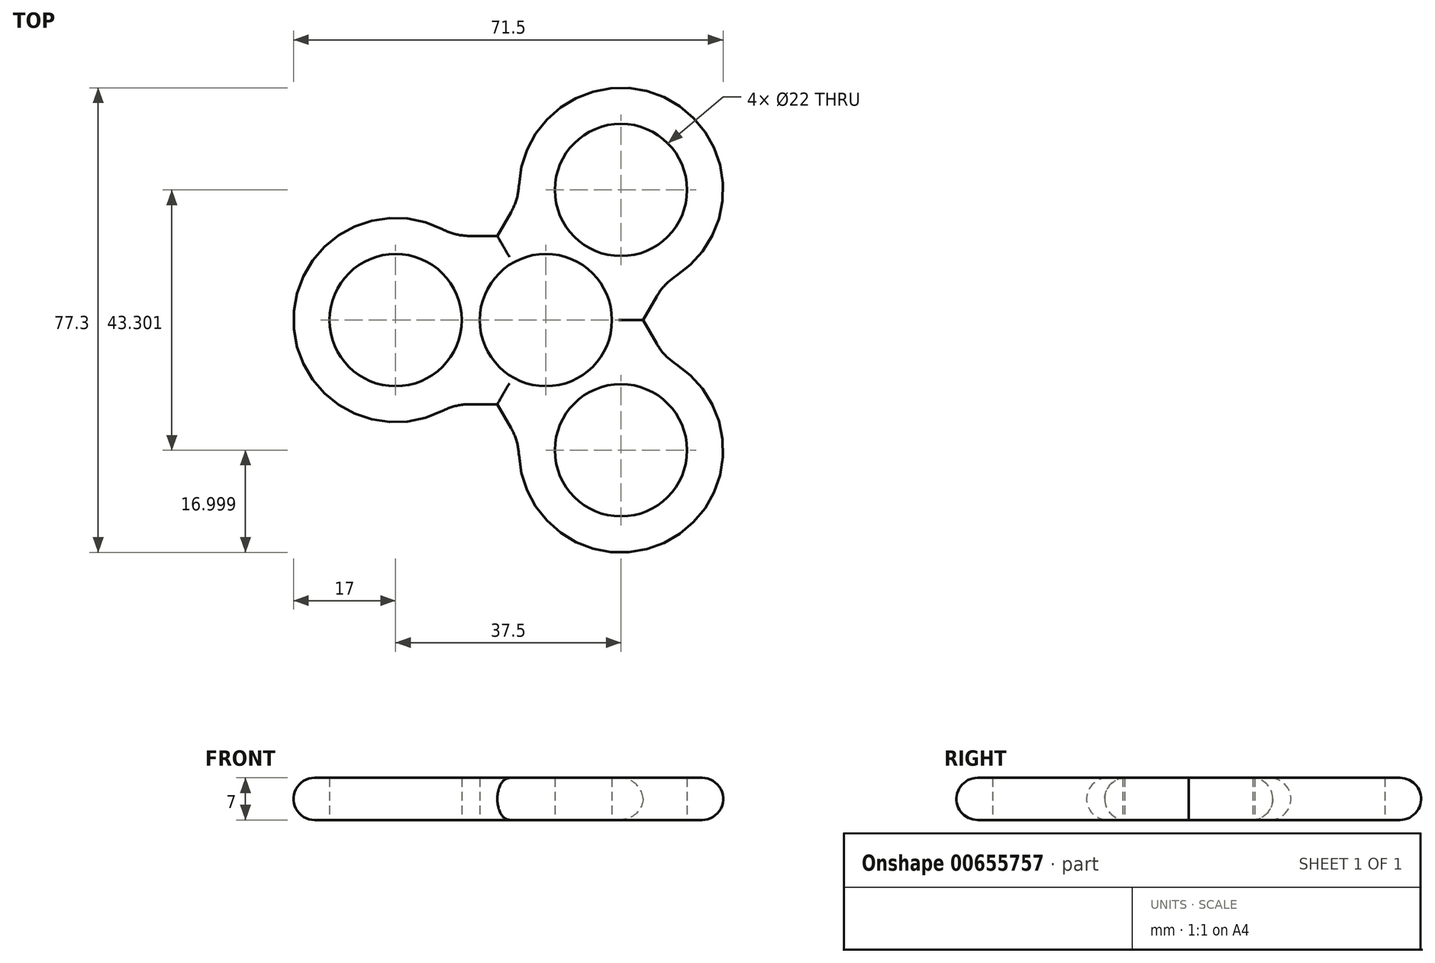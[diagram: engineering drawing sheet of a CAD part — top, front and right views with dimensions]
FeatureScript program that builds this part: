
annotation { "Feature Type Name" : "Feature", "Feature Type Description" : "" }
export const myFeature = defineFeature(function(context is Context, id is Id, definition is map)
    precondition{}
    {
        {
            var Q0;
            Q0=qCreatedBy(makeId("Top.planeOp"),FACE);
            var sketch = newSketch(context, id + "F0", { "sketchPlane" : qUnion([Q0])});
            skArc(sketch, "E0", {"start": v(0, 11) * mm, "mid": v(-11, 0) * mm, "end": v(0, -11) * mm});
            skLineSegment(sketch, "E1", {"start": v(0, 56.07) * mm, "end": v(0, 11) * mm, "construction": true});
            skLineSegment(sketch, "E2", {"start": v(-42, 56.32) * mm, "end": v(-42, -55.95) * mm, "construction": true});
            skArc(sketch, "E3", {"start": v(-15.36, 14) * mm, "mid": v(-42, 0) * mm, "end": v(-15.36, -14) * mm});
            skLineSegment(sketch, "E4", {"start": v(0, 14) * mm, "end": v(-15.36, 14) * mm});
            skLineSegment(sketch, "E5", {"start": v(0, -14) * mm, "end": v(-15.36, -14) * mm});
            skLineSegment(sketch, "E6", {"start": v(0, 14) * mm, "end": v(0, 11) * mm});
            skLineSegment(sketch, "E7.trimOffspring", {"start": v(0, -11) * mm, "end": v(0, -55.82) * mm, "construction": true});
            skLineSegment(sketch, "E8.trimOffspring", {"start": v(0, -11) * mm, "end": v(0, -14) * mm});
            skCircle(sketch, "E9", {"center": v(-25, 0) * mm, "radius": 11 * mm});
            skSolve(sketch);
        }
        {
            var Q0;
            Q0=qSketchRegion(id+"F0",true);
            extrude(context, id + "F1", {"entities" : qUnion([Q0]), "depth" : 7 * mm, "offsetDistance" : 25 * mm});
        }
        {
            var Q0;
            Q0=makeQuery(id+"F1.opExtrude","SWEPT_EDGE",EDGE,{"disambiguationData":[OSD([sQuery(id+"F0.wireOp",EDGE,"E3"),sQuery(id+"F0.wireOp",EDGE,"E5")])]});
            var Q1;
            Q1=makeQuery(id+"F1.opExtrude","SWEPT_EDGE",EDGE,{"disambiguationData":[OSD([sQuery(id+"F0.wireOp",EDGE,"E3"),sQuery(id+"F0.wireOp",EDGE,"E4")])]});
            fillet(context, id + "F2", {"entities" : qUnion([Q0, Q1]), "radius" : 10 * mm, "tangentPropagation" : true, "allowEdgeOverflow" : false});
        }
        {
            var Q0;
            Q0=qCreatedBy(makeId("Front.planeOp"),FACE);
            var sketch = newSketch(context, id + "F3", { "sketchPlane" : qUnion([Q0])});
            skLineSegment(sketch, "E10.0", {"start": v(0, 7) * mm, "end": v(0, 0) * mm});
            skSolve(sketch);
        }
        {
            var Q0;
            Q0=makeQuery(id+"F1.opExtrude","SWEPT_BODY",BODY,{"disambiguationData":[OSD([sQuery(id+"F0.wireOp",EDGE,"E0"),sQuery(id+"F0.wireOp",EDGE,"E3"),sQuery(id+"F0.wireOp",EDGE,"E4"),sQuery(id+"F0.wireOp",EDGE,"E5"),sQuery(id+"F0.wireOp",EDGE,"E6"),sQuery(id+"F0.wireOp",EDGE,"E8.trimOffspring"),sQuery(id+"F0.wireOp",EDGE,"E9")])]});
            var Q1;
            Q1=sQuery(id+"F3.wireOp",EDGE,"E10.0");
            circularPattern(context, id + "F4", {"operationType" : NewBodyOperationType.ADD, "entities" : qUnion([Q0]), "axis" : qUnion([Q1]), "angle" : 240 * degree, "instanceCount" : 3, "equalSpace" : true});
        }
        {
            var Q0;
            Q0=makeQuery(id+"F1.opExtrude","CAP_EDGE",EDGE,{"disambiguationData":[OSD([sQuery(id+"F0.wireOp",EDGE,"E3")])],"isStart":false});
            var Q1;
            {var subQ0=sQuery(id+"F0.wireOp",EDGE,"E4");var subQ1=sQuery(id+"F0.wireOp",EDGE,"E3");Q1=makeQuery(id+"F2.opFillet","BLEND_EDGE",EDGE,{"blendedFrom":[makeQuery(id+"F1.opExtrude","SWEPT_EDGE",EDGE,{"disambiguationData":[OSD([subQ1,subQ0])]}),makeQuery(id+"F1.opExtrude","CAP_FACE",FACE,{"disambiguationData":[OSD([sQuery(id+"F0.wireOp",EDGE,"E0"),subQ1,subQ0,sQuery(id+"F0.wireOp",EDGE,"E5"),sQuery(id+"F0.wireOp",EDGE,"E6"),sQuery(id+"F0.wireOp",EDGE,"E8.trimOffspring"),sQuery(id+"F0.wireOp",EDGE,"E9")])],"isStart":false})],"blendedInto":[makeQuery(id+"F1.opExtrude","CAP_FACE",FACE,{"disambiguationData":[OSD([sQuery(id+"F0.wireOp",EDGE,"E0"),subQ1,subQ0,sQuery(id+"F0.wireOp",EDGE,"E5"),sQuery(id+"F0.wireOp",EDGE,"E6"),sQuery(id+"F0.wireOp",EDGE,"E8.trimOffspring"),sQuery(id+"F0.wireOp",EDGE,"E9")])],"isStart":false})]});}
            var Q2;
            Q2=makeQuery(id+"F1.opExtrude","CAP_EDGE",EDGE,{"disambiguationData":[OSD([sQuery(id+"F0.wireOp",EDGE,"E4")])],"isStart":false});
            var Q3;
            Q3=makeQuery(id+"F4.opPattern","COPY",EDGE,{"derivedFrom":makeQuery(id+"F1.opExtrude","CAP_EDGE",EDGE,{"disambiguationData":[OSD([sQuery(id+"F0.wireOp",EDGE,"E5")])],"isStart":false}),"instanceName":"1"});
            var Q4;
            {var subQ0=sQuery(id+"F0.wireOp",EDGE,"E5");var subQ1=sQuery(id+"F0.wireOp",EDGE,"E3");Q4=makeQuery(id+"F2.opFillet","BLEND_EDGE",EDGE,{"blendedFrom":[makeQuery(id+"F1.opExtrude","SWEPT_EDGE",EDGE,{"disambiguationData":[OSD([subQ1,subQ0])]}),makeQuery(id+"F1.opExtrude","CAP_FACE",FACE,{"disambiguationData":[OSD([sQuery(id+"F0.wireOp",EDGE,"E0"),subQ1,sQuery(id+"F0.wireOp",EDGE,"E4"),subQ0,sQuery(id+"F0.wireOp",EDGE,"E6"),sQuery(id+"F0.wireOp",EDGE,"E8.trimOffspring"),sQuery(id+"F0.wireOp",EDGE,"E9")])],"isStart":false})],"blendedInto":[makeQuery(id+"F1.opExtrude","CAP_FACE",FACE,{"disambiguationData":[OSD([sQuery(id+"F0.wireOp",EDGE,"E0"),subQ1,sQuery(id+"F0.wireOp",EDGE,"E4"),subQ0,sQuery(id+"F0.wireOp",EDGE,"E6"),sQuery(id+"F0.wireOp",EDGE,"E8.trimOffspring"),sQuery(id+"F0.wireOp",EDGE,"E9")])],"isStart":false})]});}
            var Q5;
            Q5=makeQuery(id+"F1.opExtrude","CAP_EDGE",EDGE,{"disambiguationData":[OSD([sQuery(id+"F0.wireOp",EDGE,"E5")])],"isStart":false});
            var Q6;
            Q6=makeQuery(id+"F4.opPattern","COPY",EDGE,{"derivedFrom":makeQuery(id+"F1.opExtrude","CAP_EDGE",EDGE,{"disambiguationData":[OSD([sQuery(id+"F0.wireOp",EDGE,"E4")])],"isStart":false}),"instanceName":"2"});
            var Q7;
            {var subQ0=sQuery(id+"F0.wireOp",EDGE,"E4");var subQ1=sQuery(id+"F0.wireOp",EDGE,"E3");Q7=makeQuery(id+"F4.opPattern","COPY",EDGE,{"derivedFrom":makeQuery(id+"F2.opFillet","BLEND_EDGE",EDGE,{"blendedFrom":[makeQuery(id+"F1.opExtrude","SWEPT_EDGE",EDGE,{"disambiguationData":[OSD([subQ1,subQ0])]}),makeQuery(id+"F1.opExtrude","CAP_FACE",FACE,{"disambiguationData":[OSD([sQuery(id+"F0.wireOp",EDGE,"E0"),subQ1,subQ0,sQuery(id+"F0.wireOp",EDGE,"E5"),sQuery(id+"F0.wireOp",EDGE,"E6"),sQuery(id+"F0.wireOp",EDGE,"E8.trimOffspring"),sQuery(id+"F0.wireOp",EDGE,"E9")])],"isStart":false})],"blendedInto":[makeQuery(id+"F1.opExtrude","CAP_FACE",FACE,{"disambiguationData":[OSD([sQuery(id+"F0.wireOp",EDGE,"E0"),subQ1,subQ0,sQuery(id+"F0.wireOp",EDGE,"E5"),sQuery(id+"F0.wireOp",EDGE,"E6"),sQuery(id+"F0.wireOp",EDGE,"E8.trimOffspring"),sQuery(id+"F0.wireOp",EDGE,"E9")])],"isStart":false})]}),"instanceName":"2"});}
            var Q8;
            Q8=makeQuery(id+"F4.opPattern","COPY",EDGE,{"derivedFrom":makeQuery(id+"F1.opExtrude","CAP_EDGE",EDGE,{"disambiguationData":[OSD([sQuery(id+"F0.wireOp",EDGE,"E3")])],"isStart":false}),"instanceName":"2"});
            var Q9;
            {var subQ0=sQuery(id+"F0.wireOp",EDGE,"E5");var subQ1=sQuery(id+"F0.wireOp",EDGE,"E3");Q9=makeQuery(id+"F4.opPattern","COPY",EDGE,{"derivedFrom":makeQuery(id+"F2.opFillet","BLEND_EDGE",EDGE,{"blendedFrom":[makeQuery(id+"F1.opExtrude","SWEPT_EDGE",EDGE,{"disambiguationData":[OSD([subQ1,subQ0])]}),makeQuery(id+"F1.opExtrude","CAP_FACE",FACE,{"disambiguationData":[OSD([sQuery(id+"F0.wireOp",EDGE,"E0"),subQ1,sQuery(id+"F0.wireOp",EDGE,"E4"),subQ0,sQuery(id+"F0.wireOp",EDGE,"E6"),sQuery(id+"F0.wireOp",EDGE,"E8.trimOffspring"),sQuery(id+"F0.wireOp",EDGE,"E9")])],"isStart":false})],"blendedInto":[makeQuery(id+"F1.opExtrude","CAP_FACE",FACE,{"disambiguationData":[OSD([sQuery(id+"F0.wireOp",EDGE,"E0"),subQ1,sQuery(id+"F0.wireOp",EDGE,"E4"),subQ0,sQuery(id+"F0.wireOp",EDGE,"E6"),sQuery(id+"F0.wireOp",EDGE,"E8.trimOffspring"),sQuery(id+"F0.wireOp",EDGE,"E9")])],"isStart":false})]}),"instanceName":"2"});}
            var Q10;
            Q10=makeQuery(id+"F4.opPattern","COPY",EDGE,{"derivedFrom":makeQuery(id+"F1.opExtrude","CAP_EDGE",EDGE,{"disambiguationData":[OSD([sQuery(id+"F0.wireOp",EDGE,"E5")])],"isStart":false}),"instanceName":"2"});
            var Q11;
            Q11=makeQuery(id+"F4.opPattern","COPY",EDGE,{"derivedFrom":makeQuery(id+"F1.opExtrude","CAP_EDGE",EDGE,{"disambiguationData":[OSD([sQuery(id+"F0.wireOp",EDGE,"E4")])],"isStart":false}),"instanceName":"1"});
            var Q12;
            {var subQ0=sQuery(id+"F0.wireOp",EDGE,"E4");var subQ1=sQuery(id+"F0.wireOp",EDGE,"E3");Q12=makeQuery(id+"F4.opPattern","COPY",EDGE,{"derivedFrom":makeQuery(id+"F2.opFillet","BLEND_EDGE",EDGE,{"blendedFrom":[makeQuery(id+"F1.opExtrude","SWEPT_EDGE",EDGE,{"disambiguationData":[OSD([subQ1,subQ0])]}),makeQuery(id+"F1.opExtrude","CAP_FACE",FACE,{"disambiguationData":[OSD([sQuery(id+"F0.wireOp",EDGE,"E0"),subQ1,subQ0,sQuery(id+"F0.wireOp",EDGE,"E5"),sQuery(id+"F0.wireOp",EDGE,"E6"),sQuery(id+"F0.wireOp",EDGE,"E8.trimOffspring"),sQuery(id+"F0.wireOp",EDGE,"E9")])],"isStart":false})],"blendedInto":[makeQuery(id+"F1.opExtrude","CAP_FACE",FACE,{"disambiguationData":[OSD([sQuery(id+"F0.wireOp",EDGE,"E0"),subQ1,subQ0,sQuery(id+"F0.wireOp",EDGE,"E5"),sQuery(id+"F0.wireOp",EDGE,"E6"),sQuery(id+"F0.wireOp",EDGE,"E8.trimOffspring"),sQuery(id+"F0.wireOp",EDGE,"E9")])],"isStart":false})]}),"instanceName":"1"});}
            var Q13;
            Q13=makeQuery(id+"F4.opPattern","COPY",EDGE,{"derivedFrom":makeQuery(id+"F1.opExtrude","CAP_EDGE",EDGE,{"disambiguationData":[OSD([sQuery(id+"F0.wireOp",EDGE,"E3")])],"isStart":false}),"instanceName":"1"});
            var Q14;
            {var subQ0=sQuery(id+"F0.wireOp",EDGE,"E5");var subQ1=sQuery(id+"F0.wireOp",EDGE,"E3");Q14=makeQuery(id+"F4.opPattern","COPY",EDGE,{"derivedFrom":makeQuery(id+"F2.opFillet","BLEND_EDGE",EDGE,{"blendedFrom":[makeQuery(id+"F1.opExtrude","SWEPT_EDGE",EDGE,{"disambiguationData":[OSD([subQ1,subQ0])]}),makeQuery(id+"F1.opExtrude","CAP_FACE",FACE,{"disambiguationData":[OSD([sQuery(id+"F0.wireOp",EDGE,"E0"),subQ1,sQuery(id+"F0.wireOp",EDGE,"E4"),subQ0,sQuery(id+"F0.wireOp",EDGE,"E6"),sQuery(id+"F0.wireOp",EDGE,"E8.trimOffspring"),sQuery(id+"F0.wireOp",EDGE,"E9")])],"isStart":false})],"blendedInto":[makeQuery(id+"F1.opExtrude","CAP_FACE",FACE,{"disambiguationData":[OSD([sQuery(id+"F0.wireOp",EDGE,"E0"),subQ1,sQuery(id+"F0.wireOp",EDGE,"E4"),subQ0,sQuery(id+"F0.wireOp",EDGE,"E6"),sQuery(id+"F0.wireOp",EDGE,"E8.trimOffspring"),sQuery(id+"F0.wireOp",EDGE,"E9")])],"isStart":false})]}),"instanceName":"1"});}
            fillet(context, id + "F5", {"entities" : qUnion([Q0, Q1, Q2, Q3, Q4, Q5, Q6, Q7, Q8, Q9, Q10, Q11, Q12, Q13, Q14]), "radius" : 3.5 * mm, "tangentPropagation" : true, "allowEdgeOverflow" : false});
        }
        {
            var Q0;
            {var subQ0=sQuery(id+"F0.wireOp",EDGE,"E4");var subQ1=sQuery(id+"F0.wireOp",EDGE,"E3");Q0=makeQuery(id+"F4.opPattern","COPY",EDGE,{"derivedFrom":makeQuery(id+"F2.opFillet","BLEND_EDGE",EDGE,{"blendedFrom":[makeQuery(id+"F1.opExtrude","SWEPT_EDGE",EDGE,{"disambiguationData":[OSD([subQ1,subQ0])]}),makeQuery(id+"F1.opExtrude","CAP_FACE",FACE,{"disambiguationData":[OSD([sQuery(id+"F0.wireOp",EDGE,"E0"),subQ1,subQ0,sQuery(id+"F0.wireOp",EDGE,"E5"),sQuery(id+"F0.wireOp",EDGE,"E6"),sQuery(id+"F0.wireOp",EDGE,"E8.trimOffspring"),sQuery(id+"F0.wireOp",EDGE,"E9")])],"isStart":true})],"blendedInto":[makeQuery(id+"F1.opExtrude","CAP_FACE",FACE,{"disambiguationData":[OSD([sQuery(id+"F0.wireOp",EDGE,"E0"),subQ1,subQ0,sQuery(id+"F0.wireOp",EDGE,"E5"),sQuery(id+"F0.wireOp",EDGE,"E6"),sQuery(id+"F0.wireOp",EDGE,"E8.trimOffspring"),sQuery(id+"F0.wireOp",EDGE,"E9")])],"isStart":true})]}),"instanceName":"1"});}
            var Q1;
            Q1=makeQuery(id+"F4.opPattern","COPY",EDGE,{"derivedFrom":makeQuery(id+"F1.opExtrude","CAP_EDGE",EDGE,{"disambiguationData":[OSD([sQuery(id+"F0.wireOp",EDGE,"E4")])],"isStart":true}),"instanceName":"1"});
            var Q2;
            Q2=makeQuery(id+"F4.opPattern","COPY",EDGE,{"derivedFrom":makeQuery(id+"F1.opExtrude","CAP_EDGE",EDGE,{"disambiguationData":[OSD([sQuery(id+"F0.wireOp",EDGE,"E5")])],"isStart":true}),"instanceName":"2"});
            var Q3;
            {var subQ0=sQuery(id+"F0.wireOp",EDGE,"E5");var subQ1=sQuery(id+"F0.wireOp",EDGE,"E3");Q3=makeQuery(id+"F4.opPattern","COPY",EDGE,{"derivedFrom":makeQuery(id+"F2.opFillet","BLEND_EDGE",EDGE,{"blendedFrom":[makeQuery(id+"F1.opExtrude","SWEPT_EDGE",EDGE,{"disambiguationData":[OSD([subQ1,subQ0])]}),makeQuery(id+"F1.opExtrude","CAP_FACE",FACE,{"disambiguationData":[OSD([sQuery(id+"F0.wireOp",EDGE,"E0"),subQ1,sQuery(id+"F0.wireOp",EDGE,"E4"),subQ0,sQuery(id+"F0.wireOp",EDGE,"E6"),sQuery(id+"F0.wireOp",EDGE,"E8.trimOffspring"),sQuery(id+"F0.wireOp",EDGE,"E9")])],"isStart":true})],"blendedInto":[makeQuery(id+"F1.opExtrude","CAP_FACE",FACE,{"disambiguationData":[OSD([sQuery(id+"F0.wireOp",EDGE,"E0"),subQ1,sQuery(id+"F0.wireOp",EDGE,"E4"),subQ0,sQuery(id+"F0.wireOp",EDGE,"E6"),sQuery(id+"F0.wireOp",EDGE,"E8.trimOffspring"),sQuery(id+"F0.wireOp",EDGE,"E9")])],"isStart":true})]}),"instanceName":"2"});}
            var Q4;
            Q4=makeQuery(id+"F4.opPattern","COPY",EDGE,{"derivedFrom":makeQuery(id+"F1.opExtrude","CAP_EDGE",EDGE,{"disambiguationData":[OSD([sQuery(id+"F0.wireOp",EDGE,"E3")])],"isStart":true}),"instanceName":"2"});
            var Q5;
            {var subQ0=sQuery(id+"F0.wireOp",EDGE,"E4");var subQ1=sQuery(id+"F0.wireOp",EDGE,"E3");Q5=makeQuery(id+"F4.opPattern","COPY",EDGE,{"derivedFrom":makeQuery(id+"F2.opFillet","BLEND_EDGE",EDGE,{"blendedFrom":[makeQuery(id+"F1.opExtrude","SWEPT_EDGE",EDGE,{"disambiguationData":[OSD([subQ1,subQ0])]}),makeQuery(id+"F1.opExtrude","CAP_FACE",FACE,{"disambiguationData":[OSD([sQuery(id+"F0.wireOp",EDGE,"E0"),subQ1,subQ0,sQuery(id+"F0.wireOp",EDGE,"E5"),sQuery(id+"F0.wireOp",EDGE,"E6"),sQuery(id+"F0.wireOp",EDGE,"E8.trimOffspring"),sQuery(id+"F0.wireOp",EDGE,"E9")])],"isStart":true})],"blendedInto":[makeQuery(id+"F1.opExtrude","CAP_FACE",FACE,{"disambiguationData":[OSD([sQuery(id+"F0.wireOp",EDGE,"E0"),subQ1,subQ0,sQuery(id+"F0.wireOp",EDGE,"E5"),sQuery(id+"F0.wireOp",EDGE,"E6"),sQuery(id+"F0.wireOp",EDGE,"E8.trimOffspring"),sQuery(id+"F0.wireOp",EDGE,"E9")])],"isStart":true})]}),"instanceName":"2"});}
            var Q6;
            Q6=makeQuery(id+"F4.opPattern","COPY",EDGE,{"derivedFrom":makeQuery(id+"F1.opExtrude","CAP_EDGE",EDGE,{"disambiguationData":[OSD([sQuery(id+"F0.wireOp",EDGE,"E4")])],"isStart":true}),"instanceName":"2"});
            var Q7;
            Q7=makeQuery(id+"F1.opExtrude","CAP_EDGE",EDGE,{"disambiguationData":[OSD([sQuery(id+"F0.wireOp",EDGE,"E5")])],"isStart":true});
            var Q8;
            {var subQ0=sQuery(id+"F0.wireOp",EDGE,"E5");var subQ1=sQuery(id+"F0.wireOp",EDGE,"E3");Q8=makeQuery(id+"F2.opFillet","BLEND_EDGE",EDGE,{"blendedFrom":[makeQuery(id+"F1.opExtrude","SWEPT_EDGE",EDGE,{"disambiguationData":[OSD([subQ1,subQ0])]}),makeQuery(id+"F1.opExtrude","CAP_FACE",FACE,{"disambiguationData":[OSD([sQuery(id+"F0.wireOp",EDGE,"E0"),subQ1,sQuery(id+"F0.wireOp",EDGE,"E4"),subQ0,sQuery(id+"F0.wireOp",EDGE,"E6"),sQuery(id+"F0.wireOp",EDGE,"E8.trimOffspring"),sQuery(id+"F0.wireOp",EDGE,"E9")])],"isStart":true})],"blendedInto":[makeQuery(id+"F1.opExtrude","CAP_FACE",FACE,{"disambiguationData":[OSD([sQuery(id+"F0.wireOp",EDGE,"E0"),subQ1,sQuery(id+"F0.wireOp",EDGE,"E4"),subQ0,sQuery(id+"F0.wireOp",EDGE,"E6"),sQuery(id+"F0.wireOp",EDGE,"E8.trimOffspring"),sQuery(id+"F0.wireOp",EDGE,"E9")])],"isStart":true})]});}
            var Q9;
            Q9=makeQuery(id+"F1.opExtrude","CAP_EDGE",EDGE,{"disambiguationData":[OSD([sQuery(id+"F0.wireOp",EDGE,"E3")])],"isStart":true});
            var Q10;
            {var subQ0=sQuery(id+"F0.wireOp",EDGE,"E4");var subQ1=sQuery(id+"F0.wireOp",EDGE,"E3");Q10=makeQuery(id+"F2.opFillet","BLEND_EDGE",EDGE,{"blendedFrom":[makeQuery(id+"F1.opExtrude","SWEPT_EDGE",EDGE,{"disambiguationData":[OSD([subQ1,subQ0])]}),makeQuery(id+"F1.opExtrude","CAP_FACE",FACE,{"disambiguationData":[OSD([sQuery(id+"F0.wireOp",EDGE,"E0"),subQ1,subQ0,sQuery(id+"F0.wireOp",EDGE,"E5"),sQuery(id+"F0.wireOp",EDGE,"E6"),sQuery(id+"F0.wireOp",EDGE,"E8.trimOffspring"),sQuery(id+"F0.wireOp",EDGE,"E9")])],"isStart":true})],"blendedInto":[makeQuery(id+"F1.opExtrude","CAP_FACE",FACE,{"disambiguationData":[OSD([sQuery(id+"F0.wireOp",EDGE,"E0"),subQ1,subQ0,sQuery(id+"F0.wireOp",EDGE,"E5"),sQuery(id+"F0.wireOp",EDGE,"E6"),sQuery(id+"F0.wireOp",EDGE,"E8.trimOffspring"),sQuery(id+"F0.wireOp",EDGE,"E9")])],"isStart":true})]});}
            var Q11;
            Q11=makeQuery(id+"F1.opExtrude","CAP_EDGE",EDGE,{"disambiguationData":[OSD([sQuery(id+"F0.wireOp",EDGE,"E4")])],"isStart":true});
            var Q12;
            Q12=makeQuery(id+"F4.opPattern","COPY",EDGE,{"derivedFrom":makeQuery(id+"F1.opExtrude","CAP_EDGE",EDGE,{"disambiguationData":[OSD([sQuery(id+"F0.wireOp",EDGE,"E5")])],"isStart":true}),"instanceName":"1"});
            var Q13;
            {var subQ0=sQuery(id+"F0.wireOp",EDGE,"E5");var subQ1=sQuery(id+"F0.wireOp",EDGE,"E3");Q13=makeQuery(id+"F4.opPattern","COPY",EDGE,{"derivedFrom":makeQuery(id+"F2.opFillet","BLEND_EDGE",EDGE,{"blendedFrom":[makeQuery(id+"F1.opExtrude","SWEPT_EDGE",EDGE,{"disambiguationData":[OSD([subQ1,subQ0])]}),makeQuery(id+"F1.opExtrude","CAP_FACE",FACE,{"disambiguationData":[OSD([sQuery(id+"F0.wireOp",EDGE,"E0"),subQ1,sQuery(id+"F0.wireOp",EDGE,"E4"),subQ0,sQuery(id+"F0.wireOp",EDGE,"E6"),sQuery(id+"F0.wireOp",EDGE,"E8.trimOffspring"),sQuery(id+"F0.wireOp",EDGE,"E9")])],"isStart":true})],"blendedInto":[makeQuery(id+"F1.opExtrude","CAP_FACE",FACE,{"disambiguationData":[OSD([sQuery(id+"F0.wireOp",EDGE,"E0"),subQ1,sQuery(id+"F0.wireOp",EDGE,"E4"),subQ0,sQuery(id+"F0.wireOp",EDGE,"E6"),sQuery(id+"F0.wireOp",EDGE,"E8.trimOffspring"),sQuery(id+"F0.wireOp",EDGE,"E9")])],"isStart":true})]}),"instanceName":"1"});}
            var Q14;
            Q14=makeQuery(id+"F4.opPattern","COPY",EDGE,{"derivedFrom":makeQuery(id+"F1.opExtrude","CAP_EDGE",EDGE,{"disambiguationData":[OSD([sQuery(id+"F0.wireOp",EDGE,"E3")])],"isStart":true}),"instanceName":"1"});
            fillet(context, id + "F6", {"entities" : qUnion([Q0, Q1, Q2, Q3, Q4, Q5, Q6, Q7, Q8, Q9, Q10, Q11, Q12, Q13, Q14]), "radius" : 3.5 * mm, "tangentPropagation" : true, "allowEdgeOverflow" : false});
        }
    });
